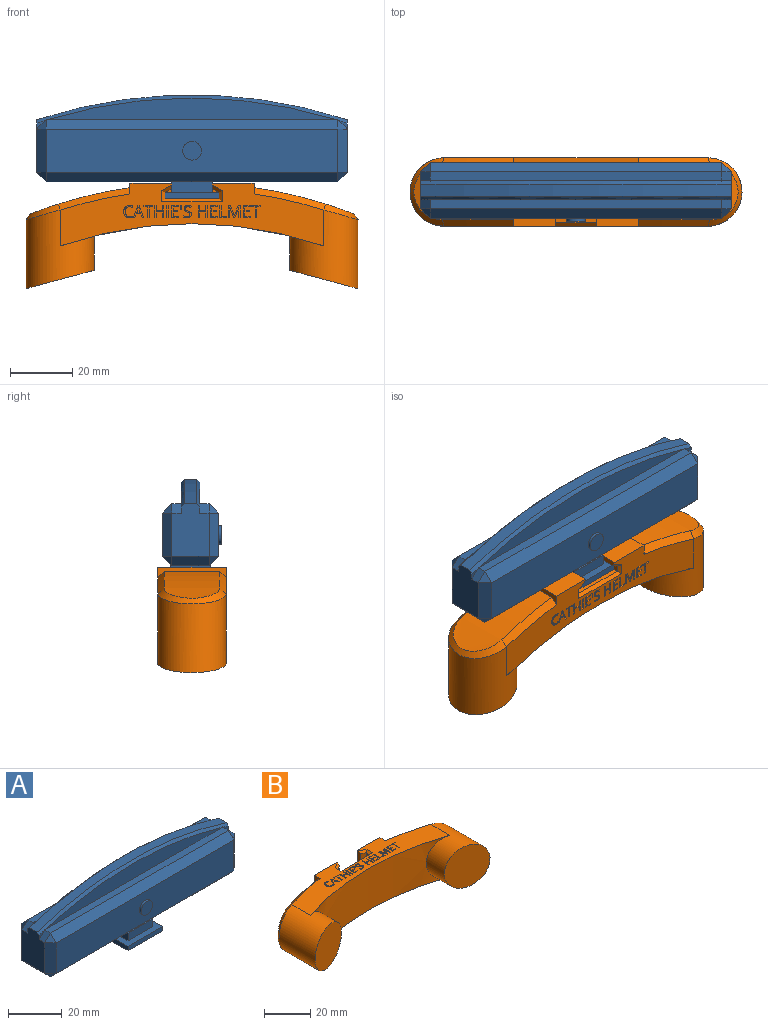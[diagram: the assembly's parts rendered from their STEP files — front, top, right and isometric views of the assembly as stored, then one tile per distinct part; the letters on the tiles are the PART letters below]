
ASSEMBLY  parts=2 mates=1
PART A: 53 faces, bbox 100.6x19x33.5 mm
  f0: plane 40.5x12mm, normal (0,0,-1), area 486mm2, adj f21,f31,f35,f43
  f1: plane 2.86x2.86mm, normal (0,-1,0), area 2.8mm2, adj f8,f19,f38
  f2: plane 93.39x7mm, normal (0,-1,0), area 437.8mm2, adj f6,f38
  f3: plane 2.86x2.86mm, normal (0,1,0), area 2.8mm2, adj f10,f16,f37
  f4: plane 93.39x7mm, normal (0,1,0), area 437.8mm2, adj f11,f37
  f5: plane 2.86x2.86mm, normal (0,-1,0), area 2.8mm2, adj f10,f23,f38
  f6: plane 94x3.09mm, normal (0,0,1), area 282mm2, adj f2,f19,f23,f24,f38
  f7: plane 94x14mm, normal (0,-1,0), area 1287.7mm2, adj f24,f29,f32,f35,f51
  f8: plane 17x12mm, normal (1,0,0), area 184.9mm2, adj f1,f13,f14,f19,f20,f29,f30,f36
  f9: plane 94x14mm, normal (0,1,0), area 1316mm2, adj f15,f20,f21,f22
  f10: plane 17x12mm, normal (-1,0,0), area 184.9mm2, adj f3,f5,f16,f22,f23,f31,f32,f36
  f11: plane 94x3.09mm, normal (0,0,1), area 282mm2, adj f4,f14,f15,f16,f37
  f12: plane 40.5x12mm, normal (0,0,-1), area 486mm2, adj f21,f30,f35,f41
  f13: plane 2.86x2.86mm, normal (0,1,0), area 2.8mm2, adj f8,f14,f37
  f14: plane 3.09x3mm, normal (0.71,0,0.71), area 12.7mm2, adj f8,f11,f13,f17,f37
  f15: plane 94x3mm, normal (0,0.71,0.71), area 398.8mm2, adj f9,f11,f17,f18
  f16: plane 3.09x3mm, normal (-0.71,0,0.71), area 12.7mm2, adj f3,f10,f11,f18,f37
  f17: plane 3x3mm, normal (0.58,0.58,0.58), area 7.8mm2, adj f14,f15,f20
  f18: plane 3x3mm, normal (-0.58,0.58,0.58), area 7.8mm2, adj f15,f16,f22
  f19: plane 3.09x3mm, normal (0.71,0,0.71), area 12.7mm2, adj f1,f6,f8,f25,f38
  f20: plane 14x3mm, normal (0.71,0.71,0), area 59.4mm2, adj f8,f9,f17,f26
  f21: plane 94x3mm, normal (0,0.71,-0.71), area 398.8mm2, adj f0,f9,f12,f26,f27,f44
  f22: plane 14x3mm, normal (-0.71,0.71,0), area 59.4mm2, adj f9,f10,f18,f27
  f23: plane 3.09x3mm, normal (-0.71,0,0.71), area 12.7mm2, adj f5,f6,f10,f28,f38
  f24: plane 94x3mm, normal (0,-0.71,0.71), area 398.8mm2, adj f6,f7,f25,f28
  f25: plane 3x3mm, normal (0.58,-0.58,0.58), area 7.8mm2, adj f19,f24,f29
  f26: plane 3x3mm, normal (0.58,0.58,-0.58), area 7.8mm2, adj f20,f21,f30
  f27: plane 3x3mm, normal (-0.58,0.58,-0.58), area 7.8mm2, adj f21,f22,f31
  f28: plane 3x3mm, normal (-0.58,-0.58,0.58), area 7.8mm2, adj f23,f24,f32
  f29: plane 14x3mm, normal (0.71,-0.71,0), area 59.4mm2, adj f7,f8,f25,f33
  f30: plane 12x3mm, normal (0.71,0,-0.71), area 50.9mm2, adj f8,f12,f26,f33
  f31: plane 12x3mm, normal (-0.71,0,-0.71), area 50.9mm2, adj f0,f10,f27,f34
  f32: plane 14x3mm, normal (-0.71,-0.71,0), area 59.4mm2, adj f7,f10,f28,f34
  f33: plane 3x3mm, normal (0.58,-0.58,-0.58), area 7.8mm2, adj f29,f30,f35
  f34: plane 3x3mm, normal (-0.58,-0.58,-0.58), area 7.8mm2, adj f31,f32,f35
  f35: plane 94x3mm, normal (0,-0.71,-0.71), area 398.8mm2, adj f0,f7,f12,f33,f34,f39
  f36: cylinder r=160.25mm len=100mm, axis (0,-1,0), area 406.8mm2, adj f8,f10,f37,f38
  f37: cone r=159.25mm half-angle=45deg, axis (0,-1,0), area 143.8mm2, adj f3,f4,f8,f10,f11,f13,f14,f16
  f38: cone r=159.25mm half-angle=45deg, axis (0,1,0), area 143.8mm2, adj f1,f2,f5,f6,f8,f10,f19,f23
  f39: plane 13x0.5mm, normal (0,0,1), area 6.5mm2, adj f35,f40,f41,f43
  f40: plane 13x3.5mm, normal (0,-1,0), area 45.5mm2, adj f39,f41,f43,f45
  f41: plane 13x3.5mm, normal (1,0,0), area 45.5mm2, adj f12,f39,f40,f42,f44,f45
  f42: plane 13x3.5mm, normal (0,1,0), area 45.5mm2, adj f41,f43,f44,f45
  f43: plane 13x3.5mm, normal (-1,0,0), area 45.5mm2, adj f0,f39,f40,f42,f44,f45
  f44: plane 13x0.5mm, normal (0,0,1), area 6.5mm2, adj f21,f41,f42,f43
  f45: plane 18x18mm, normal (0,0,1), area 155mm2, adj f40,f41,f42,f43,f46,f47,f48,f49
  f46: plane 18x2mm, normal (0,1,0), area 36mm2, adj f45,f47,f49,f50
  f47: plane 18x2mm, normal (1,0,0), area 36mm2, adj f45,f46,f48,f50
  f48: plane 18x2mm, normal (0,-1,0), area 36mm2, adj f45,f47,f49,f50
  f49: plane 18x2mm, normal (-1,0,0), area 36mm2, adj f45,f46,f48,f50
  f50: plane 18x18mm, normal (0,0,-1), area 324mm2, adj f46,f47,f48,f49
  f51: cylinder r=3mm len=6mm, axis (0,1,0), area 18.8mm2, adj f7,f52
  f52: plane 6x6mm, normal (0,-1,0), area 28.3mm2, adj f51
PART B: 207 faces, bbox 115x41.9x30 mm
  f0: cylinder r=11mm len=22.36mm, axis (0,1,0), area 1042mm2, adj f1,f2,f5,f6,f200
  f1: plane 30.03x30.03mm, normal (0.26,-0.97,0), area 393.7mm2, adj f0
  f2: cylinder r=129.17mm len=85mm, axis (0,0,-1), area 1507.7mm2, adj f0,f3,f5,f6
  f3: cylinder r=11mm len=22.36mm, axis (0,1,0), area 1042mm2, adj f2,f4,f5,f6,f197
  f4: plane 30.03x30.03mm, normal (-0.26,-0.97,0), area 393.7mm2, adj f3
  f5: plane 85x20.19mm, normal (0,0,1), area 895.7mm2, adj f0,f2,f3,f7,f8,f9,f12,f18
  f6: plane 85x20.19mm, normal (0,0,-1), area 1050.4mm2, adj f0,f2,f3,f7,f8,f9,f198,f201
  f7: plane 22x3.44mm, normal (1,0,0), area 35.1mm2, adj f5,f6,f9,f11,f196,f198
  f8: plane 22x3.44mm, normal (-1,0,0), area 35.1mm2, adj f5,f6,f9,f10,f199,f201
  f9: plane 40x22mm, normal (0,1,0), area 620mm2, adj f5,f6,f7,f8,f12,f16,f18
  f10: cylinder r=142.17mm len=32.24mm, axis (0,0,-1), area 563.9mm2, adj f8,f199,f200,f201
  f11: cylinder r=142.17mm len=32.24mm, axis (0,0,-1), area 563.9mm2, adj f7,f196,f197,f198
  f12: plane 20x1.7mm, normal (1,0,0), area 33.4mm2, adj f5,f9,f13,f16,f206
  f13: plane 19x2.25mm, normal (0.5,-0.87,0), area 49.4mm2, adj f12,f14,f16,f206
  f14: plane 19x2mm, normal (1,0,0), area 38mm2, adj f13,f15,f16,f205
  f15: plane 19x17.5mm, normal (0,1,0), area 332.5mm2, adj f14,f16,f17,f204
  f16: plane 17.5x5mm, normal (0,0,1), area 76.9mm2, adj f9,f12,f13,f14,f15,f17,f18,f19
  f17: plane 19x2mm, normal (-1,0,0), area 38mm2, adj f15,f16,f19,f203
  f18: plane 20x1.7mm, normal (-1,0,0), area 33.4mm2, adj f5,f9,f16,f19,f202
  f19: plane 19x2.25mm, normal (-0.5,-0.87,0), area 49.4mm2, adj f16,f17,f18,f202
  f20: plane 3.84x2.88mm, normal (0,0,1), area 2.7mm2, adj f21,f22,f23,f24,f25,f26,f27,f28
  f21: plane 0.5x0.45mm, normal (0,1,0), area 0.2mm2, adj f5,f20,f22,f28
  f22: plane 3.45x0.5mm, normal (-1,0,0), area 1.7mm2, adj f5,f20,f21,f23
  f23: plane 1.22x0.5mm, normal (0,1,0), area 0.6mm2, adj f5,f20,f22,f24
  f24: plane 0.5x0.4mm, normal (-1,0,0), area 0.2mm2, adj f5,f20,f23,f25
  f25: plane 2.88x0.5mm, normal (0,-1,0), area 1.4mm2, adj f5,f20,f24,f26
  f26: plane 0.5x0.4mm, normal (1,0,0), area 0.2mm2, adj f5,f20,f25,f27
  f27: plane 1.22x0.5mm, normal (0,1,0), area 0.6mm2, adj f5,f20,f26,f28
  f28: plane 3.45x0.5mm, normal (1,0,0), area 1.7mm2, adj f5,f20,f21,f27
  f29: plane 3.84x2.92mm, normal (0,0,1), area 4.2mm2, adj f30,f31,f32,f33,f34,f35,f36,f37
  f30: plane 0.5x0.45mm, normal (0,1,0), area 0.2mm2, adj f5,f29,f31,f41
  f31: plane 3.84x0.5mm, normal (-1,0,0), area 1.9mm2, adj f5,f29,f30,f32
  f32: plane 0.5x0.45mm, normal (0,-1,0), area 0.2mm2, adj f5,f29,f31,f33
  f33: plane 1.63x0.5mm, normal (1,0,0), area 0.8mm2, adj f5,f29,f32,f34
  f34: plane 2.02x0.5mm, normal (0,-1,0), area 1mm2, adj f5,f29,f33,f35
  f35: plane 1.63x0.5mm, normal (-1,0,0), area 0.8mm2, adj f5,f29,f34,f36
  f36: plane 0.5x0.45mm, normal (0,-1,0), area 0.2mm2, adj f5,f29,f35,f37
  f37: plane 3.84x0.5mm, normal (1,0,0), area 1.9mm2, adj f5,f29,f36,f38
  f38: plane 0.5x0.45mm, normal (0,1,0), area 0.2mm2, adj f5,f29,f37,f39
  f39: plane 1.81x0.5mm, normal (-1,0,0), area 0.9mm2, adj f5,f29,f38,f40
  f40: plane 2.02x0.5mm, normal (0,1,0), area 1mm2, adj f5,f29,f39,f41
  f41: plane 1.81x0.5mm, normal (1,0,0), area 0.9mm2, adj f5,f29,f30,f40
  f42: plane 3.84x0.45mm, normal (0,0,1), area 1.7mm2, adj f43,f44,f45,f46
  f43: plane 3.84x0.5mm, normal (1,0,0), area 1.9mm2, adj f5,f42,f44,f46
  f44: plane 0.5x0.45mm, normal (0,1,0), area 0.2mm2, adj f5,f42,f43,f45
  f45: plane 3.84x0.5mm, normal (-1,0,0), area 1.9mm2, adj f5,f42,f44,f46
  f46: plane 0.5x0.45mm, normal (0,-1,0), area 0.2mm2, adj f5,f42,f43,f45
  f47: plane 3.84x2.14mm, normal (0,0,1), area 3.7mm2, adj f48,f49,f50,f51,f52,f53,f54,f55
  f48: plane 2.14x0.5mm, normal (0,1,0), area 1.1mm2, adj f5,f47,f49,f59
  f49: plane 0.5x0.4mm, normal (-1,0,0), area 0.2mm2, adj f5,f47,f48,f50
  f50: plane 1.7x0.5mm, normal (0,-1,0), area 0.8mm2, adj f5,f47,f49,f51
  f51: plane 1.41x0.5mm, normal (-1,0,0), area 0.7mm2, adj f5,f47,f50,f52
  f52: plane 1.59x0.5mm, normal (0,1,0), area 0.8mm2, adj f5,f47,f51,f53
  f53: plane 0.5x0.39mm, normal (-1,0,0), area 0.2mm2, adj f5,f47,f52,f54
  f54: plane 1.59x0.5mm, normal (0,-1,0), area 0.8mm2, adj f5,f47,f53,f55
  f55: plane 1.24x0.5mm, normal (-1,0,0), area 0.6mm2, adj f5,f47,f54,f56
  f56: plane 1.7x0.5mm, normal (0,1,0), area 0.8mm2, adj f5,f47,f55,f57
  f57: plane 0.5x0.4mm, normal (-1,0,0), area 0.2mm2, adj f5,f47,f56,f58
  f58: plane 2.14x0.5mm, normal (0,-1,0), area 1.1mm2, adj f5,f47,f57,f59
  f59: plane 3.84x0.5mm, normal (1,0,0), area 1.9mm2, adj f5,f47,f48,f58
  f60: plane 1.39x0.49mm, normal (0,0,1), area 0.5mm2, adj f61,f62,f63,f64
  f61: plane 1.39x0.5mm, normal (-1,0.08,0), area 0.7mm2, adj f5,f60,f62,f64
  f62: plane 0.5x0.49mm, normal (0,-1,0), area 0.2mm2, adj f5,f60,f61,f63
  f63: plane 1.39x0.5mm, normal (1,0.08,0), area 0.7mm2, adj f5,f60,f62,f64
  f64: plane 0.5x0.28mm, normal (0,1,0), area 0.1mm2, adj f5,f60,f61,f63
  f65: plane 3.95x2.42mm, normal (0,0,1), area 3.4mm2, adj f66,f67,f68,f69,f70,f71,f72,f73
  f66: extruded ~0.79x0.5mm, area 0.5mm2, adj f5,f65,f67,f90
  f67: extruded ~0.64x0.5mm, area 0.3mm2, adj f5,f65,f66,f68
  f68: extruded ~0.83x0.5mm, area 0.5mm2, adj f5,f65,f67,f69
  f69: extruded ~0.54x0.5mm, area 0.3mm2, adj f5,f65,f68,f70
  f70: extruded ~0.5x0.25mm, area 0.2mm2, adj f5,f65,f69,f71
  f71: extruded ~0.5x0.33mm, area 0.2mm2, adj f5,f65,f70,f72
  f72: extruded ~0.5x0.42mm, area 0.2mm2, adj f5,f65,f71,f73
  f73: extruded ~0.55x0.5mm, area 0.3mm2, adj f5,f65,f72,f74
  f74: extruded ~0.93x0.5mm, area 0.5mm2, adj f5,f65,f73,f75
  f75: plane 0.5x0.39mm, normal (-0.94,0.34,0), area 0.2mm2, adj f5,f65,f74,f76
  f76: extruded ~1.05x0.5mm, area 0.5mm2, adj f5,f65,f75,f77
  f77: extruded ~0.88x0.5mm, area 0.5mm2, adj f5,f65,f76,f78
  f78: extruded ~0.71x0.5mm, area 0.4mm2, adj f5,f65,f77,f79
  f79: extruded ~0.69x0.5mm, area 0.4mm2, adj f5,f65,f78,f80
  f80: extruded ~0.77x0.5mm, area 0.4mm2, adj f5,f65,f79,f81
  f81: extruded ~0.57x0.5mm, area 0.3mm2, adj f5,f65,f80,f82
  f82: extruded ~0.5x0.27mm, area 0.2mm2, adj f5,f65,f81,f83
  f83: extruded ~0.5x0.33mm, area 0.2mm2, adj f5,f65,f82,f84
  f84: extruded ~0.5x0.47mm, area 0.3mm2, adj f5,f65,f83,f85
  f85: extruded ~0.67x0.5mm, area 0.4mm2, adj f5,f65,f84,f86
  f86: extruded ~0.55x0.5mm, area 0.3mm2, adj f5,f65,f85,f87
  f87: extruded ~0.52x0.5mm, area 0.3mm2, adj f5,f65,f86,f88
  f88: plane 0.5x0.43mm, normal (1,0,0), area 0.2mm2, adj f5,f65,f87,f89
  f89: extruded ~1.05x0.5mm, area 0.5mm2, adj f5,f65,f88,f90
  f90: extruded ~1x0.5mm, area 0.5mm2, adj f5,f65,f66,f89
  f91: plane 3.84x2.92mm, normal (0,0,1), area 4.2mm2, adj f92,f93,f94,f95,f96,f97,f98,f99
  f92: plane 0.5x0.45mm, normal (0,1,0), area 0.2mm2, adj f5,f91,f93,f103
  f93: plane 3.84x0.5mm, normal (-1,0,0), area 1.9mm2, adj f5,f91,f92,f94
  f94: plane 0.5x0.45mm, normal (0,-1,0), area 0.2mm2, adj f5,f91,f93,f95
  f95: plane 1.63x0.5mm, normal (1,0,0), area 0.8mm2, adj f5,f91,f94,f96
  f96: plane 2.02x0.5mm, normal (0,-1,0), area 1mm2, adj f5,f91,f95,f97
  f97: plane 1.63x0.5mm, normal (-1,0,0), area 0.8mm2, adj f5,f91,f96,f98
  f98: plane 0.5x0.45mm, normal (0,-1,0), area 0.2mm2, adj f5,f91,f97,f99
  f99: plane 3.84x0.5mm, normal (1,0,0), area 1.9mm2, adj f5,f91,f98,f100
  f100: plane 0.5x0.45mm, normal (0,1,0), area 0.2mm2, adj f5,f91,f99,f101
  f101: plane 1.81x0.5mm, normal (-1,0,0), area 0.9mm2, adj f5,f91,f100,f102
  f102: plane 2.02x0.5mm, normal (0,1,0), area 1mm2, adj f5,f91,f101,f103
  f103: plane 1.81x0.5mm, normal (1,0,0), area 0.9mm2, adj f5,f91,f92,f102
  f104: plane 3.84x2.14mm, normal (0,0,1), area 3.7mm2, adj f105,f106,f107,f108,f109,f110,f111,f112
  f105: plane 2.14x0.5mm, normal (0,1,0), area 1.1mm2, adj f5,f104,f106,f116
  f106: plane 0.5x0.4mm, normal (-1,0,0), area 0.2mm2, adj f5,f104,f105,f107
  f107: plane 1.7x0.5mm, normal (0,-1,0), area 0.8mm2, adj f5,f104,f106,f108
  f108: plane 1.41x0.5mm, normal (-1,0,0), area 0.7mm2, adj f5,f104,f107,f109
  f109: plane 1.59x0.5mm, normal (0,1,0), area 0.8mm2, adj f5,f104,f108,f110
  f110: plane 0.5x0.39mm, normal (-1,0,0), area 0.2mm2, adj f5,f104,f109,f111
  f111: plane 1.59x0.5mm, normal (0,-1,0), area 0.8mm2, adj f5,f104,f110,f112
  f112: plane 1.24x0.5mm, normal (-1,0,0), area 0.6mm2, adj f5,f104,f111,f113
  f113: plane 1.7x0.5mm, normal (0,1,0), area 0.8mm2, adj f5,f104,f112,f114
  f114: plane 0.5x0.4mm, normal (-1,0,0), area 0.2mm2, adj f5,f104,f113,f115
  f115: plane 2.14x0.5mm, normal (0,-1,0), area 1.1mm2, adj f5,f104,f114,f116
  f116: plane 3.84x0.5mm, normal (1,0,0), area 1.9mm2, adj f5,f104,f105,f115
  f117: plane 3.84x2.14mm, normal (0,0,1), area 2.4mm2, adj f118,f119,f120,f121,f122,f123
  f118: plane 3.84x0.5mm, normal (1,0,0), area 1.9mm2, adj f5,f117,f119,f123
  f119: plane 2.14x0.5mm, normal (0,1,0), area 1.1mm2, adj f5,f117,f118,f120
  f120: plane 0.5x0.4mm, normal (-1,0,0), area 0.2mm2, adj f5,f117,f119,f121
  f121: plane 1.7x0.5mm, normal (0,-1,0), area 0.8mm2, adj f5,f117,f120,f122
  f122: plane 3.44x0.5mm, normal (-1,0,0), area 1.7mm2, adj f5,f117,f121,f123
  f123: plane 0.5x0.45mm, normal (0,-1,0), area 0.2mm2, adj f5,f117,f118,f122
  f124: plane 3.84x3.81mm, normal (0,0,1), area 6.3mm2, adj f125,f126,f127,f128,f129,f130,f131,f132
  f125: plane 3.41x1.3mm, normal (0.93,0.36,0), area 1.8mm2, adj f5,f124,f126,f142
  f126: plane 0.5x0.36mm, normal (0,1,0), area 0.2mm2, adj f5,f124,f125,f127
  f127: plane 3.4x1.31mm, normal (-0.93,0.36,0), area 1.8mm2, adj f5,f124,f126,f128
  f128: plane 0.5x0.02mm, normal (0,1,0), area 0mm2, adj f5,f124,f127,f129
  f129: extruded ~0.93x0.5mm, area 0.5mm2, adj f5,f124,f128,f130
  f130: plane 2.48x0.5mm, normal (1,0,0), area 1.2mm2, adj f5,f124,f129,f131
  f131: plane 0.5x0.45mm, normal (0,1,0), area 0.2mm2, adj f5,f124,f130,f132
  f132: plane 3.84x0.5mm, normal (-1,0,0), area 1.9mm2, adj f5,f124,f131,f133
  f133: plane 0.67x0.5mm, normal (0,-1,0), area 0.3mm2, adj f5,f124,f132,f134
  f134: plane 3.17x1.23mm, normal (0.93,-0.36,0), area 1.7mm2, adj f5,f124,f133,f135
  f135: plane 0.5x0.02mm, normal (0,-1,0), area 0mm2, adj f5,f124,f134,f136
  f136: plane 3.17x1.22mm, normal (-0.93,-0.36,0), area 1.7mm2, adj f5,f124,f135,f137
  f137: plane 0.67x0.5mm, normal (0,-1,0), area 0.3mm2, adj f5,f124,f136,f138
  f138: plane 3.84x0.5mm, normal (1,0,0), area 1.9mm2, adj f5,f124,f137,f139
  f139: plane 0.5x0.41mm, normal (0,1,0), area 0.2mm2, adj f5,f124,f138,f140
  f140: plane 2.44x0.5mm, normal (-1,0,0), area 1.2mm2, adj f5,f124,f139,f141
  f141: extruded ~0.96x0.5mm, area 0.5mm2, adj f5,f124,f140,f142
  f142: plane 0.5x0.02mm, normal (0,1,0), area 0mm2, adj f5,f124,f125,f141
  f143: plane 3.84x2.14mm, normal (0,0,1), area 3.7mm2, adj f144,f145,f146,f147,f148,f149,f150,f151
  f144: plane 2.14x0.5mm, normal (0,1,0), area 1.1mm2, adj f5,f143,f145,f155
  f145: plane 0.5x0.4mm, normal (-1,0,0), area 0.2mm2, adj f5,f143,f144,f146
  f146: plane 1.7x0.5mm, normal (0,-1,0), area 0.8mm2, adj f5,f143,f145,f147
  f147: plane 1.41x0.5mm, normal (-1,0,0), area 0.7mm2, adj f5,f143,f146,f148
  f148: plane 1.59x0.5mm, normal (0,1,0), area 0.8mm2, adj f5,f143,f147,f149
  f149: plane 0.5x0.39mm, normal (-1,0,0), area 0.2mm2, adj f5,f143,f148,f150
  f150: plane 1.59x0.5mm, normal (0,-1,0), area 0.8mm2, adj f5,f143,f149,f151
  f151: plane 1.24x0.5mm, normal (-1,0,0), area 0.6mm2, adj f5,f143,f150,f152
  f152: plane 1.7x0.5mm, normal (0,1,0), area 0.8mm2, adj f5,f143,f151,f153
  f153: plane 0.5x0.4mm, normal (-1,0,0), area 0.2mm2, adj f5,f143,f152,f154
  f154: plane 2.14x0.5mm, normal (0,-1,0), area 1.1mm2, adj f5,f143,f153,f155
  f155: plane 3.84x0.5mm, normal (1,0,0), area 1.9mm2, adj f5,f143,f144,f154
  f156: plane 3.84x2.88mm, normal (0,0,1), area 2.7mm2, adj f157,f158,f159,f160,f161,f162,f163,f164
  f157: plane 3.45x0.5mm, normal (-1,0,0), area 1.7mm2, adj f5,f156,f158,f162
  f158: plane 1.22x0.5mm, normal (0,1,0), area 0.6mm2, adj f5,f156,f157,f159
  f159: plane 0.5x0.4mm, normal (-1,0,0), area 0.2mm2, adj f5,f156,f158,f160
  f160: plane 2.88x0.5mm, normal (0,-1,0), area 1.4mm2, adj f5,f156,f159,f161
  f161: plane 0.5x0.4mm, normal (1,0,0), area 0.2mm2, adj f5,f156,f160,f163
  f162: plane 0.5x0.45mm, normal (0,1,0), area 0.2mm2, adj f5,f156,f157,f164
  f163: plane 1.22x0.5mm, normal (0,1,0), area 0.6mm2, adj f5,f156,f161,f164
  f164: plane 3.45x0.5mm, normal (1,0,0), area 1.7mm2, adj f5,f156,f162,f163
  f165: plane 3.86x3.41mm, normal (0,0,1), area 3.8mm2, adj f166,f167,f168,f169,f170,f171,f172,f173
  f166: plane 1.24x0.5mm, normal (0,-1,0), area 0.6mm2, adj f165,f167,f173,f179
  f167: plane 1.19x0.5mm, normal (-0.94,0.35,0), area 0.6mm2, adj f165,f166,f174,f179
  f168: plane 0.5x0.46mm, normal (0,1,0), area 0.2mm2, adj f5,f165,f169,f176
  f169: plane 3.86x1.51mm, normal (-0.93,-0.36,0), area 2.1mm2, adj f5,f165,f168,f170
  f170: plane 0.5x0.38mm, normal (0,-1,0), area 0.2mm2, adj f5,f165,f169,f171
  f171: plane 3.86x1.52mm, normal (0.93,-0.37,0), area 2.1mm2, adj f5,f165,f170,f172
  f172: plane 0.5x0.45mm, normal (0,1,0), area 0.2mm2, adj f5,f165,f171,f177
  f173: plane 1.19x0.5mm, normal (0.94,0.35,0), area 0.6mm2, adj f165,f166,f175,f179
  f174: extruded ~0.55x0.5mm, area 0.3mm2, adj f165,f167,f175,f179
  f175: extruded ~0.55x0.5mm, area 0.3mm2, adj f165,f173,f174,f179
  f176: plane 1.22x0.5mm, normal (0.93,0.36,0), area 0.7mm2, adj f5,f165,f168,f178
  f177: plane 1.22x0.5mm, normal (-0.93,0.36,0), area 0.7mm2, adj f5,f165,f172,f178
  f178: plane 1.54x0.5mm, normal (0,1,0), area 0.8mm2, adj f5,f165,f176,f177
  f179: plane 1.75x1.24mm, normal (0,0,1), area 1mm2, adj f166,f167,f173,f174,f175
  f180: plane 3.95x2.91mm, normal (0,0,1), area 3.2mm2, adj f181,f182,f183,f184,f185,f186,f187,f188
  f181: extruded ~0.87x0.5mm, area 0.5mm2, adj f5,f180,f182,f193
  f182: plane 0.5x0.38mm, normal (-0.9,0.44,0), area 0.2mm2, adj f5,f180,f181,f183
  f183: extruded ~1.06x0.5mm, area 0.5mm2, adj f5,f180,f182,f184
  f184: extruded ~0.99x0.5mm, area 0.5mm2, adj f5,f180,f183,f185
  f185: extruded ~0.69x0.64mm, area 0.5mm2, adj f5,f180,f184,f186
  f186: extruded ~1.04x0.5mm, area 0.5mm2, adj f5,f180,f185,f187
  f187: extruded ~1.46x0.5mm, area 0.8mm2, adj f5,f180,f186,f188
  f188: extruded ~1.31x0.52mm, area 0.7mm2, adj f5,f180,f187,f189
  f189: extruded ~0.99x0.5mm, area 0.5mm2, adj f5,f180,f188,f190
  f190: plane 0.5x0.39mm, normal (-1,0,0), area 0.2mm2, adj f5,f180,f189,f191
  f191: extruded ~0.92x0.5mm, area 0.5mm2, adj f5,f180,f190,f192
  f192: extruded ~1.01x0.5mm, area 0.6mm2, adj f5,f180,f191,f194
  f193: extruded ~1x0.5mm, area 0.6mm2, adj f5,f180,f181,f195
  f194: extruded ~1.17x0.5mm, area 0.6mm2, adj f5,f180,f192,f195
  f195: extruded ~1.16x0.5mm, area 0.6mm2, adj f5,f180,f193,f194
  f196: cone r=142.17mm half-angle=45deg, axis (0,0,-1), area 66.2mm2, adj f5,f7,f11,f197
  f197: bspline ~22x11mm, area 80.3mm2, adj f3,f11,f196,f198
  f198: cone r=140.17mm half-angle=45deg, axis (0,0,1), area 66.2mm2, adj f6,f7,f11,f197
  f199: cone r=142.17mm half-angle=45deg, axis (0,0,-1), area 66.2mm2, adj f5,f8,f10,f200
  f200: bspline ~22x11mm, area 80.3mm2, adj f0,f10,f199,f201
  f201: cone r=140.17mm half-angle=45deg, axis (0,0,1), area 66.2mm2, adj f6,f8,f10,f200
  f202: plane 3.25x2.45mm, normal (-0.35,-0.61,0.71), area 4.5mm2, adj f5,f18,f19,f203
  f203: plane 3.58x1mm, normal (-0.71,0,0.71), area 3.9mm2, adj f5,f17,f202,f204
  f204: plane 19.5x1mm, normal (0,0.71,0.71), area 26.2mm2, adj f5,f15,f203,f205
  f205: plane 3.58x1mm, normal (0.71,0,0.71), area 3.9mm2, adj f5,f14,f204,f206
  f206: plane 3.25x2.45mm, normal (0.35,-0.61,0.71), area 4.5mm2, adj f5,f12,f13,f205
PLACE A t=(-21.64,16.92,9.29)mm
PLACE B rot(axis=(1,0,0),90deg) t=(-21.64,16.42,-4.21)mm fixed
MATE planar B.f15 <-> A.f50  axis (0,0,1) through (-21.64,15.92,3.79)mm
